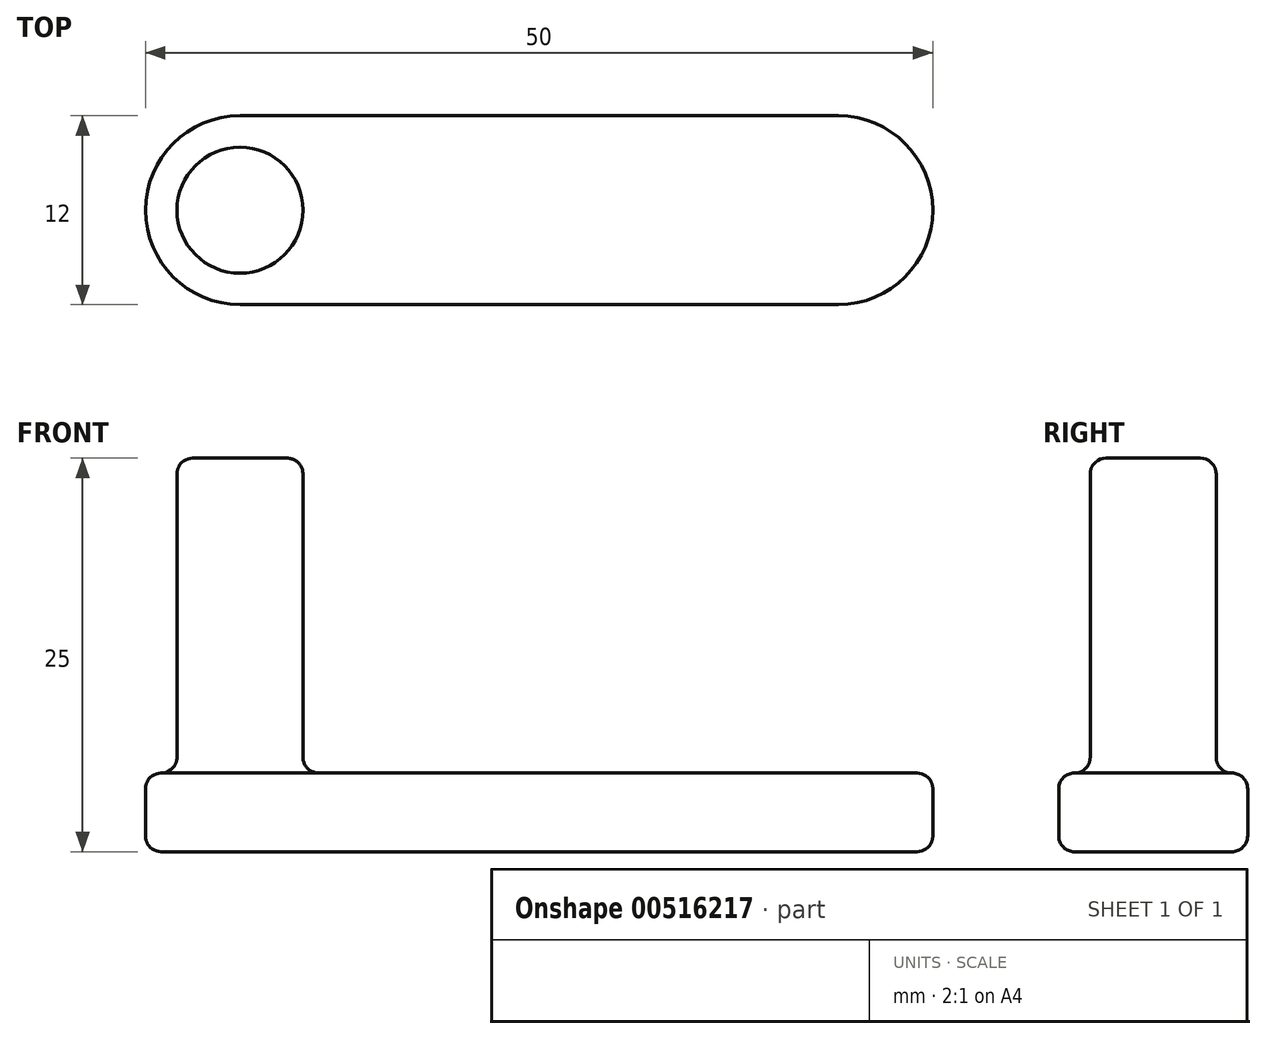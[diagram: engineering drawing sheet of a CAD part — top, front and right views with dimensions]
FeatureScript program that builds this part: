
annotation { "Feature Type Name" : "Feature", "Feature Type Description" : "" }
export const myFeature = defineFeature(function(context is Context, id is Id, definition is map)
    precondition{}
    {
        {
            var Q0;
            Q0=qCreatedBy(makeId("Top.planeOp"),FACE);
            var sketch = newSketch(context, id + "F0", { "sketchPlane" : qUnion([Q0])});
            skLineSegment(sketch, "E0.bottom", {"start": v(19, 6) * mm, "end": v(-19, 6) * mm});
            skLineSegment(sketch, "E0.top", {"start": v(19, -6) * mm, "end": v(-19, -6) * mm});
            skLineSegment(sketch, "E0.left", {"start": v(25, 0) * mm, "end": v(25, 0) * mm});
            skLineSegment(sketch, "E0.right", {"start": v(-25, 0) * mm, "end": v(-25, 0) * mm});
            skPoint(sketch, "E0.middle", {"position": v(0, 0) * mm});
            skPoint(sketch, "E1.visualSharp", {"position": v(-25, 6) * mm});
            skArc(sketch, "E1.filletArc", {"start": v(-19, 6) * mm, "mid": v(-23.24, 4.24) * mm, "end": v(-25, 0) * mm});
            skPoint(sketch, "E2.visualSharp", {"position": v(-25, -6) * mm});
            skArc(sketch, "E2.filletArc", {"start": v(-25, 0) * mm, "mid": v(-23.24, -4.24) * mm, "end": v(-19, -6) * mm});
            skPoint(sketch, "E3.visualSharp", {"position": v(25, -6) * mm});
            skArc(sketch, "E3.filletArc", {"start": v(19, -6) * mm, "mid": v(23.24, -4.24) * mm, "end": v(25, 0) * mm});
            skPoint(sketch, "E4.visualSharp", {"position": v(25, 6) * mm});
            skArc(sketch, "E4.filletArc", {"start": v(25, 0) * mm, "mid": v(23.24, 4.24) * mm, "end": v(19, 6) * mm});
            skCircle(sketch, "E5", {"center": v(-19, 0) * mm, "radius": 4 * mm});
            skCircle(sketch, "E6", {"center": v(19, 0) * mm, "radius": 4 * mm});
            skSolve(sketch);
        }
        {
            var Q0;
            Q0=makeQuery(id+"F0.imprint","IMPRINT",FACE,{"disambiguationData":[TD([[makeQuery(id+"F0.imprint","IMPRINT",EDGE,{"derivedFrom":sQuery(id+"F0.wireOp",EDGE,"E0.bottom")}),1.0]])]});
            var Q1;
            Q1=makeQuery(id+"F0.imprint","IMPRINT",FACE,{"disambiguationData":[TD([[makeQuery(id+"F0.imprint","IMPRINT",EDGE,{"derivedFrom":sQuery(id+"F0.wireOp",EDGE,"E5")}),1.0]])]});
            var Q2;
            Q2=makeQuery(id+"F0.imprint","IMPRINT",FACE,{"disambiguationData":[TD([[makeQuery(id+"F0.imprint","IMPRINT",EDGE,{"derivedFrom":sQuery(id+"F0.wireOp",EDGE,"E6")}),1.0]])]});
            extrude(context, id + "F1", {"entities" : qUnion([Q0, Q1, Q2]), "depth" : 5 * mm, "offsetDistance" : 25 * mm});
        }
        {
            var Q0;
            Q0=makeQuery(id+"F0.imprint","IMPRINT",FACE,{"disambiguationData":[TD([[makeQuery(id+"F0.imprint","IMPRINT",EDGE,{"derivedFrom":sQuery(id+"F0.wireOp",EDGE,"E5")}),1.0]])]});
            extrude(context, id + "F2", {"entities" : qUnion([Q0]), "operationType" : NewBodyOperationType.ADD, "depth" : 25 * mm, "offsetDistance" : 25 * mm});
        }
        {
            var Q0;
            Q0=makeQuery(id+"F1.opExtrude","CAP_EDGE",EDGE,{"disambiguationData":[OSD([sQuery(id+"F0.wireOp",EDGE,"E0.bottom")])],"isStart":false});
            var Q1;
            Q1=makeQuery(id+"F1.opExtrude","CAP_EDGE",EDGE,{"disambiguationData":[OSD([sQuery(id+"F0.wireOp",EDGE,"E0.bottom")])],"isStart":true});
            var Q2;
            Q2=makeQuery(id+"F2.boolean.opBoolean","INTERSECT",EDGE,{"derivedFrom":[makeQuery(id+"F1.opExtrude","CAP_FACE",FACE,{"disambiguationData":[OSD([sQuery(id+"F0.wireOp",EDGE,"E0.bottom"),sQuery(id+"F0.wireOp",EDGE,"E0.top"),sQuery(id+"F0.wireOp",EDGE,"E1.filletArc"),sQuery(id+"F0.wireOp",EDGE,"E2.filletArc"),sQuery(id+"F0.wireOp",EDGE,"E3.filletArc"),sQuery(id+"F0.wireOp",EDGE,"E4.filletArc")])],"isStart":false}),makeQuery(id+"F2.opExtrude","SWEPT_FACE",FACE,{"disambiguationData":[OSD([sQuery(id+"F0.wireOp",EDGE,"E5")])]})]});
            var Q3;
            Q3=makeQuery(id+"F2.opExtrude","CAP_EDGE",EDGE,{"disambiguationData":[OSD([sQuery(id+"F0.wireOp",EDGE,"E5")])],"isStart":false});
            fillet(context, id + "F3", {"entities" : qUnion([Q0, Q1, Q2, Q3]), "radius" : 1 * mm, "tangentPropagation" : true, "allowEdgeOverflow" : false});
        }
    });
